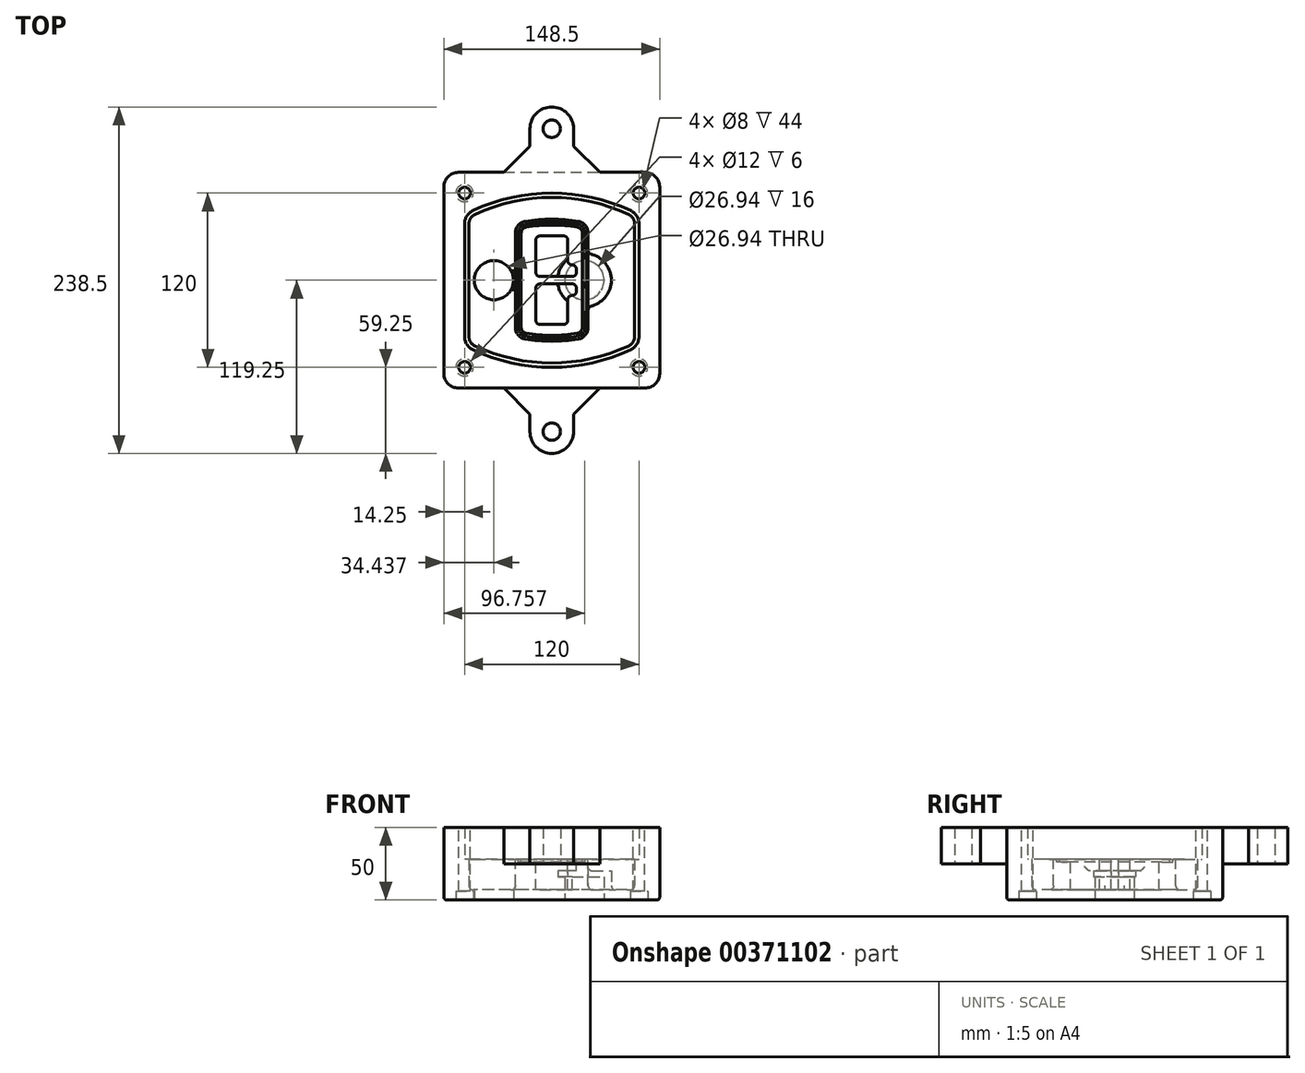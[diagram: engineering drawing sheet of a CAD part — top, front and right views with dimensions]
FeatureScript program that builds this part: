
annotation { "Feature Type Name" : "Feature", "Feature Type Description" : "" }
export const myFeature = defineFeature(function(context is Context, id is Id, definition is map)
    precondition{}
    {
        {
            var Q0;
            Q0=qCreatedBy(makeId("Top.planeOp"),FACE);
            var sketch = newSketch(context, id + "F0", { "sketchPlane" : qUnion([Q0])});
            skPoint(sketch, "E0.rect.middle", {"position": v(0, 0) * mm});
            skLineSegment(sketch, "E1.bottom", {"start": v(-64.25, -74.25) * mm, "end": v(64.25, -74.25) * mm});
            skLineSegment(sketch, "E1.top", {"start": v(-64.25, 74.25) * mm, "end": v(64.25, 74.25) * mm});
            skLineSegment(sketch, "E1.left", {"start": v(-74.25, -64.25) * mm, "end": v(-74.25, 64.25) * mm});
            skLineSegment(sketch, "E1.right", {"start": v(74.25, -64.25) * mm, "end": v(74.25, 64.25) * mm});
            skLineSegment(sketch, "E2", {"start": v(-74.25, 74.25) * mm, "end": v(74.25, -74.25) * mm, "construction": true});
            skLineSegment(sketch, "E3", {"start": v(74.25, 74.25) * mm, "end": v(-74.25, -74.25) * mm, "construction": true});
            skCircle(sketch, "E4", {"center": v(-60, 60) * mm, "radius": 4 * mm});
            skCircle(sketch, "E5", {"center": v(60, 60) * mm, "radius": 4 * mm});
            skCircle(sketch, "E6", {"center": v(60, -60) * mm, "radius": 4 * mm});
            skCircle(sketch, "E7", {"center": v(-60, -60) * mm, "radius": 4 * mm});
            skLineSegment(sketch, "E8", {"start": v(-60, 60) * mm, "end": v(60, 60) * mm, "construction": true});
            skLineSegment(sketch, "E9", {"start": v(60, 60) * mm, "end": v(60, -60) * mm, "construction": true});
            skLineSegment(sketch, "E10", {"start": v(60, -60) * mm, "end": v(-60, -60) * mm, "construction": true});
            skLineSegment(sketch, "E11", {"start": v(-60, -60) * mm, "end": v(-60, 60) * mm, "construction": true});
            skLineSegment(sketch, "E12", {"start": v(-60, 38.83) * mm, "end": v(-60, -38.83) * mm});
            skLineSegment(sketch, "E13", {"start": v(60, 38.83) * mm, "end": v(60, -38.83) * mm});
            skArc(sketch, "E14", {"start": v(54.26, 47.88) * mm, "mid": v(0, 60) * mm, "end": v(-54.26, 47.88) * mm});
            skArc(sketch, "E15", {"start": v(-54.26, -47.88) * mm, "mid": v(0, -60) * mm, "end": v(54.26, -47.88) * mm});
            skLineSegment(sketch, "E16", {"start": v(-60, 0) * mm, "end": v(60, 0) * mm, "construction": true});
            skPoint(sketch, "E17.visualSharp", {"position": v(-60, -45) * mm});
            skArc(sketch, "E17.filletArc", {"start": v(-60, -38.83) * mm, "mid": v(-58.44, -44.2) * mm, "end": v(-54.26, -47.88) * mm});
            skPoint(sketch, "E18.visualSharp", {"position": v(-60, 45) * mm});
            skArc(sketch, "E18.filletArc", {"start": v(-54.26, 47.88) * mm, "mid": v(-58.44, 44.2) * mm, "end": v(-60, 38.83) * mm});
            skPoint(sketch, "E19.visualSharp", {"position": v(60, 45) * mm});
            skArc(sketch, "E19.filletArc", {"start": v(60, 38.83) * mm, "mid": v(58.44, 44.2) * mm, "end": v(54.26, 47.88) * mm});
            skPoint(sketch, "E20.visualSharp", {"position": v(60, -45) * mm});
            skArc(sketch, "E20.filletArc", {"start": v(54.26, -47.88) * mm, "mid": v(58.44, -44.2) * mm, "end": v(60, -38.83) * mm});
            skPoint(sketch, "E21.visualSharp", {"position": v(-74.25, 74.25) * mm});
            skArc(sketch, "E21.filletArc", {"start": v(-64.25, 74.25) * mm, "mid": v(-71.32, 71.32) * mm, "end": v(-74.25, 64.25) * mm});
            skPoint(sketch, "E22.visualSharp", {"position": v(74.25, 74.25) * mm});
            skArc(sketch, "E22.filletArc", {"start": v(74.25, 64.25) * mm, "mid": v(71.32, 71.32) * mm, "end": v(64.25, 74.25) * mm});
            skPoint(sketch, "E23.visualSharp", {"position": v(74.25, -74.25) * mm});
            skArc(sketch, "E23.filletArc", {"start": v(64.25, -74.25) * mm, "mid": v(71.32, -71.32) * mm, "end": v(74.25, -64.25) * mm});
            skPoint(sketch, "E24.visualSharp", {"position": v(-74.25, -74.25) * mm});
            skArc(sketch, "E24.filletArc", {"start": v(-74.25, -64.25) * mm, "mid": v(-71.32, -71.32) * mm, "end": v(-64.25, -74.25) * mm});
            skArc(sketch, "E25.0", {"start": v(57, 38.83) * mm, "mid": v(55.9, 42.58) * mm, "end": v(52.98, 45.17) * mm});
            skLineSegment(sketch, "E25.1", {"start": v(57, 38.83) * mm, "end": v(57, -38.83) * mm});
            skArc(sketch, "E25.2", {"start": v(52.98, -45.17) * mm, "mid": v(55.9, -42.58) * mm, "end": v(57, -38.83) * mm});
            skArc(sketch, "E25.3", {"start": v(-52.98, -45.17) * mm, "mid": v(0, -57) * mm, "end": v(52.98, -45.17) * mm});
            skArc(sketch, "E25.4", {"start": v(-57, -38.83) * mm, "mid": v(-55.9, -42.58) * mm, "end": v(-52.98, -45.17) * mm});
            skArc(sketch, "E25.5", {"start": v(52.98, 45.17) * mm, "mid": v(0, 57) * mm, "end": v(-52.98, 45.17) * mm});
            skLineSegment(sketch, "E25.6", {"start": v(-57, 38.83) * mm, "end": v(-57, -38.83) * mm});
            skArc(sketch, "E25.7", {"start": v(-52.98, 45.17) * mm, "mid": v(-55.9, 42.58) * mm, "end": v(-57, 38.83) * mm});
            skArc(sketch, "E26.0", {"start": v(-55.96, 51.5) * mm, "mid": v(-61.82, 46.33) * mm, "end": v(-64, 38.83) * mm});
            skArc(sketch, "E26.1", {"start": v(55.96, 51.5) * mm, "mid": v(0, 64) * mm, "end": v(-55.96, 51.5) * mm});
            skArc(sketch, "E26.2", {"start": v(64, 38.83) * mm, "mid": v(61.82, 46.33) * mm, "end": v(55.96, 51.5) * mm});
            skLineSegment(sketch, "E26.3", {"start": v(64, 38.83) * mm, "end": v(64, -38.83) * mm});
            skArc(sketch, "E26.4", {"start": v(55.96, -51.5) * mm, "mid": v(61.82, -46.33) * mm, "end": v(64, -38.83) * mm});
            skLineSegment(sketch, "E26.5", {"start": v(-64, 38.83) * mm, "end": v(-64, -38.83) * mm});
            skArc(sketch, "E26.6", {"start": v(-55.96, -51.5) * mm, "mid": v(0, -64) * mm, "end": v(55.96, -51.5) * mm});
            skArc(sketch, "E26.7", {"start": v(-64, -38.83) * mm, "mid": v(-61.82, -46.33) * mm, "end": v(-55.96, -51.5) * mm});
            skSolve(sketch);
        }
        {
            var Q0;
            Q0=makeQuery(id+"F0.imprint","IMPRINT",FACE,{"disambiguationData":[TD([[makeQuery(id+"F0.imprint","IMPRINT",EDGE,{"derivedFrom":sQuery(id+"F0.wireOp",EDGE,"E1.bottom")}),1.0]])]});
            var Q1;
            Q1=makeQuery(id+"F0.imprint","IMPRINT",FACE,{"disambiguationData":[TD([[makeQuery(id+"F0.imprint","IMPRINT",EDGE,{"derivedFrom":sQuery(id+"F0.wireOp",EDGE,"E12")}),1.0]])]});
            var Q2;
            Q2=makeQuery(id+"F0.imprint","IMPRINT",FACE,{"disambiguationData":[TD([[makeQuery(id+"F0.imprint","IMPRINT",EDGE,{"derivedFrom":sQuery(id+"F0.wireOp",EDGE,"E25.0")}),1.0]])]});
            var Q3;
            Q3=makeQuery(id+"F0.imprint","IMPRINT",FACE,{"disambiguationData":[TD([[makeQuery(id+"F0.imprint","IMPRINT",EDGE,{"derivedFrom":sQuery(id+"F0.wireOp",EDGE,"E12")}),-1.0]])]});
            extrude(context, id + "F1", {"entities" : qUnion([Q0, Q1, Q2, Q3]), "oppositeDirection" : true, "depth" : 25 * mm});
        }
        {
            var Q0;
            Q0=makeQuery(id+"F0.imprint","IMPRINT",FACE,{"disambiguationData":[TD([[makeQuery(id+"F0.imprint","IMPRINT",EDGE,{"derivedFrom":sQuery(id+"F0.wireOp",EDGE,"E12")}),1.0]])]});
            extrude(context, id + "F2", {"entities" : qUnion([Q0]), "operationType" : NewBodyOperationType.ADD, "depth" : 3 * mm});
        }
        {
            var Q0;
            Q0=makeQuery(id+"F0.imprint","IMPRINT",FACE,{"disambiguationData":[TD([[makeQuery(id+"F0.imprint","IMPRINT",EDGE,{"derivedFrom":sQuery(id+"F0.wireOp",EDGE,"E25.0")}),1.0]])]});
            extrude(context, id + "F3", {"entities" : qUnion([Q0]), "operationType" : NewBodyOperationType.REMOVE, "oppositeDirection" : true, "depth" : 18 * mm});
        }
        {
            var Q0;
            Q0=makeQuery(id+"F2.opExtrude","CAP_FACE",FACE,{"disambiguationData":[OSD([sQuery(id+"F0.wireOp",EDGE,"E12"),sQuery(id+"F0.wireOp",EDGE,"E13"),sQuery(id+"F0.wireOp",EDGE,"E14"),sQuery(id+"F0.wireOp",EDGE,"E15"),sQuery(id+"F0.wireOp",EDGE,"E17.filletArc"),sQuery(id+"F0.wireOp",EDGE,"E18.filletArc"),sQuery(id+"F0.wireOp",EDGE,"E19.filletArc"),sQuery(id+"F0.wireOp",EDGE,"E20.filletArc"),sQuery(id+"F0.wireOp",EDGE,"E25.0"),sQuery(id+"F0.wireOp",EDGE,"E25.1"),sQuery(id+"F0.wireOp",EDGE,"E25.2"),sQuery(id+"F0.wireOp",EDGE,"E25.3"),sQuery(id+"F0.wireOp",EDGE,"E25.4"),sQuery(id+"F0.wireOp",EDGE,"E25.5"),sQuery(id+"F0.wireOp",EDGE,"E25.6"),sQuery(id+"F0.wireOp",EDGE,"E25.7")])],"isStart":false});
            var sketch = newSketch(context, id + "F4", { "sketchPlane" : qUnion([Q0])});
            skArc(sketch, "E27.0", {"start": v(-18.34, -40.45) * mm, "mid": v(0, -42) * mm, "end": v(18.34, -40.45) * mm});
            skArc(sketch, "E28.0", {"start": v(18.34, 40.45) * mm, "mid": v(0, 42) * mm, "end": v(-18.34, 40.45) * mm});
            skLineSegment(sketch, "E29", {"start": v(-25, 32.57) * mm, "end": v(-25, -32.57) * mm});
            skLineSegment(sketch, "E30", {"start": v(25, 32.57) * mm, "end": v(25, -32.57) * mm});
            skLineSegment(sketch, "E31", {"start": v(-25, 39.1) * mm, "end": v(25, 39.1) * mm, "construction": true});
            skLineSegment(sketch, "E32", {"start": v(-25, -39.1) * mm, "end": v(25, -39.1) * mm, "construction": true});
            skPoint(sketch, "E33.visualSharp", {"position": v(-25, 39.1) * mm});
            skArc(sketch, "E33.filletArc", {"start": v(-18.34, 40.45) * mm, "mid": v(-23.11, 37.73) * mm, "end": v(-25, 32.57) * mm});
            skPoint(sketch, "E34.visualSharp", {"position": v(25, 39.1) * mm});
            skArc(sketch, "E34.filletArc", {"start": v(25, 32.57) * mm, "mid": v(23.11, 37.73) * mm, "end": v(18.34, 40.45) * mm});
            skPoint(sketch, "E35.visualSharp", {"position": v(25, -39.1) * mm});
            skArc(sketch, "E35.filletArc", {"start": v(18.34, -40.45) * mm, "mid": v(23.11, -37.73) * mm, "end": v(25, -32.57) * mm});
            skPoint(sketch, "E36.visualSharp", {"position": v(-25, -39.1) * mm});
            skArc(sketch, "E36.filletArc", {"start": v(-25, -32.57) * mm, "mid": v(-23.11, -37.73) * mm, "end": v(-18.34, -40.45) * mm});
            skArc(sketch, "E37.0", {"start": v(52.98, 45.17) * mm, "mid": v(0, 57) * mm, "end": v(-52.98, 45.17) * mm});
            skArc(sketch, "E37.1", {"start": v(-52.98, 45.17) * mm, "mid": v(-55.9, 42.58) * mm, "end": v(-57, 38.83) * mm});
            skLineSegment(sketch, "E37.2", {"start": v(-57, 38.83) * mm, "end": v(-57, -38.83) * mm});
            skArc(sketch, "E37.3", {"start": v(-57, -38.83) * mm, "mid": v(-55.9, -42.58) * mm, "end": v(-52.98, -45.17) * mm});
            skArc(sketch, "E37.4", {"start": v(-52.98, -45.17) * mm, "mid": v(0, -57) * mm, "end": v(52.98, -45.17) * mm});
            skArc(sketch, "E37.5", {"start": v(52.98, -45.17) * mm, "mid": v(55.9, -42.58) * mm, "end": v(57, -38.83) * mm});
            skLineSegment(sketch, "E37.6", {"start": v(57, 38.83) * mm, "end": v(57, -38.83) * mm});
            skArc(sketch, "E37.7", {"start": v(57, 38.83) * mm, "mid": v(55.9, 42.58) * mm, "end": v(52.98, 45.17) * mm});
            skLineSegment(sketch, "E38.0", {"start": v(23, 32.57) * mm, "end": v(23, -32.57) * mm});
            skArc(sketch, "E38.1", {"start": v(18, -38.48) * mm, "mid": v(21.58, -36.44) * mm, "end": v(23, -32.57) * mm});
            skArc(sketch, "E38.2", {"start": v(-18, -38.48) * mm, "mid": v(0, -40) * mm, "end": v(18, -38.48) * mm});
            skArc(sketch, "E38.3", {"start": v(-23, -32.57) * mm, "mid": v(-21.58, -36.44) * mm, "end": v(-18, -38.48) * mm});
            skLineSegment(sketch, "E38.4", {"start": v(-23, 32.57) * mm, "end": v(-23, -32.57) * mm});
            skArc(sketch, "E38.5", {"start": v(23, 32.57) * mm, "mid": v(21.58, 36.44) * mm, "end": v(18, 38.48) * mm});
            skArc(sketch, "E38.6", {"start": v(-18, 38.48) * mm, "mid": v(-21.58, 36.44) * mm, "end": v(-23, 32.57) * mm});
            skArc(sketch, "E38.7", {"start": v(18, 38.48) * mm, "mid": v(0, 40) * mm, "end": v(-18, 38.48) * mm});
            skArc(sketch, "E39.0", {"start": v(21, 32.57) * mm, "mid": v(20.06, 35.15) * mm, "end": v(17.67, 36.5) * mm});
            skLineSegment(sketch, "E39.1", {"start": v(21, 32.57) * mm, "end": v(21, -32.57) * mm});
            skArc(sketch, "E39.2", {"start": v(17.67, -36.5) * mm, "mid": v(20.06, -35.15) * mm, "end": v(21, -32.57) * mm});
            skArc(sketch, "E39.3", {"start": v(-17.67, -36.5) * mm, "mid": v(0, -38) * mm, "end": v(17.67, -36.5) * mm});
            skArc(sketch, "E39.4", {"start": v(-21, -32.57) * mm, "mid": v(-20.06, -35.15) * mm, "end": v(-17.67, -36.5) * mm});
            skArc(sketch, "E39.5", {"start": v(17.67, 36.5) * mm, "mid": v(0, 38) * mm, "end": v(-17.67, 36.5) * mm});
            skLineSegment(sketch, "E39.6", {"start": v(-21, 32.57) * mm, "end": v(-21, -32.57) * mm});
            skArc(sketch, "E39.7", {"start": v(-17.67, 36.5) * mm, "mid": v(-20.06, 35.15) * mm, "end": v(-21, 32.57) * mm});
            skLineSegment(sketch, "E40", {"start": v(-25, 0) * mm, "end": v(25, 0) * mm, "construction": true});
            skLineSegment(sketch, "E41", {"start": v(-11, 5.5) * mm, "end": v(-11, 27.5) * mm});
            skLineSegment(sketch, "E42", {"start": v(-8, 30.5) * mm, "end": v(8, 30.5) * mm});
            skLineSegment(sketch, "E43", {"start": v(11, 27.5) * mm, "end": v(11, 13.5) * mm});
            skLineSegment(sketch, "E44", {"start": v(14, 10.5) * mm, "end": v(14, 10.5) * mm});
            skLineSegment(sketch, "E45", {"start": v(17, 7.5) * mm, "end": v(17, 5.5) * mm});
            skLineSegment(sketch, "E46", {"start": v(14, 2.5) * mm, "end": v(-8, 2.5) * mm});
            skPoint(sketch, "E47.visualSharp", {"position": v(-11, 30.5) * mm});
            skArc(sketch, "E47.filletArc", {"start": v(-8, 30.5) * mm, "mid": v(-10.12, 29.62) * mm, "end": v(-11, 27.5) * mm});
            skPoint(sketch, "E48.visualSharp", {"position": v(11, 30.5) * mm});
            skArc(sketch, "E48.filletArc", {"start": v(11, 27.5) * mm, "mid": v(10.12, 29.62) * mm, "end": v(8, 30.5) * mm});
            skPoint(sketch, "E49.visualSharp", {"position": v(11, 10.5) * mm});
            skArc(sketch, "E49.filletArc", {"start": v(11, 13.5) * mm, "mid": v(11.88, 11.38) * mm, "end": v(14, 10.5) * mm});
            skPoint(sketch, "E50.visualSharp", {"position": v(17, 10.5) * mm});
            skArc(sketch, "E50.filletArc", {"start": v(17, 7.5) * mm, "mid": v(16.12, 9.62) * mm, "end": v(14, 10.5) * mm});
            skPoint(sketch, "E51.visualSharp", {"position": v(17, 2.5) * mm});
            skArc(sketch, "E51.filletArc", {"start": v(14, 2.5) * mm, "mid": v(16.12, 3.38) * mm, "end": v(17, 5.5) * mm});
            skPoint(sketch, "E52.visualSharp", {"position": v(-11, 2.5) * mm});
            skArc(sketch, "E52.filletArc", {"start": v(-11, 5.5) * mm, "mid": v(-10.12, 3.38) * mm, "end": v(-8, 2.5) * mm});
            skLineSegment(sketch, "E53.0.MirrorCS", {"start": v(14, -2.5) * mm, "end": v(-8, -2.5) * mm});
            skArc(sketch, "E54.0.MirrorCS", {"start": v(-11, -5.5) * mm, "mid": v(-10.12, -3.38) * mm, "end": v(-8, -2.5) * mm});
            skLineSegment(sketch, "E55.0.MirrorCS", {"start": v(-11, -5.5) * mm, "end": v(-11, -27.5) * mm});
            skArc(sketch, "E56.0.MirrorCS", {"start": v(-8, -30.5) * mm, "mid": v(-10.12, -29.62) * mm, "end": v(-11, -27.5) * mm});
            skLineSegment(sketch, "E57.0.MirrorCS", {"start": v(-8, -30.5) * mm, "end": v(8, -30.5) * mm});
            skArc(sketch, "E58.0.MirrorCS", {"start": v(11, -27.5) * mm, "mid": v(10.12, -29.62) * mm, "end": v(8, -30.5) * mm});
            skLineSegment(sketch, "E59.0.MirrorCS", {"start": v(11, -27.5) * mm, "end": v(11, -13.5) * mm});
            skArc(sketch, "E60.0.MirrorCS", {"start": v(11, -13.5) * mm, "mid": v(11.88, -11.38) * mm, "end": v(14, -10.5) * mm});
            skArc(sketch, "E61.0.MirrorCS", {"start": v(17, -7.5) * mm, "mid": v(16.12, -9.62) * mm, "end": v(14, -10.5) * mm});
            skLineSegment(sketch, "E62.0.MirrorCS", {"start": v(17, -7.5) * mm, "end": v(17, -5.5) * mm});
            skArc(sketch, "E63.0.MirrorCS", {"start": v(14, -2.5) * mm, "mid": v(16.12, -3.38) * mm, "end": v(17, -5.5) * mm});
            skSolve(sketch);
        }
        {
            var Q0;
            Q0=makeQuery(id+"F4.imprint","IMPRINT",FACE,{"disambiguationData":[TD([[makeQuery(id+"F4.imprint","IMPRINT",EDGE,{"derivedFrom":sQuery(id+"F4.wireOp",EDGE,"E27.0")}),1.0]])]});
            var Q1;
            Q1=makeQuery(id+"F4.imprint","IMPRINT",FACE,{"disambiguationData":[TD([[makeQuery(id+"F4.imprint","IMPRINT",EDGE,{"derivedFrom":sQuery(id+"F4.wireOp",EDGE,"E38.0")}),-1.0]])]});
            var Q2;
            Q2=makeQuery(id+"F4.imprint","IMPRINT",FACE,{"disambiguationData":[TD([[makeQuery(id+"F4.imprint","IMPRINT",EDGE,{"derivedFrom":sQuery(id+"F4.wireOp",EDGE,"E39.0")}),1.0]])]});
            extrude(context, id + "F5", {"entities" : qUnion([Q0, Q1, Q2]), "operationType" : NewBodyOperationType.ADD, "endBound" : BoundingType.UP_TO_NEXT, "oppositeDirection" : true, "depth" : 25 * mm});
        }
        {
            var Q0;
            Q0=makeQuery(id+"F4.imprint","IMPRINT",FACE,{"disambiguationData":[TD([[makeQuery(id+"F4.imprint","IMPRINT",EDGE,{"derivedFrom":sQuery(id+"F4.wireOp",EDGE,"E38.0")}),-1.0]])]});
            extrude(context, id + "F6", {"entities" : qUnion([Q0]), "operationType" : NewBodyOperationType.REMOVE, "oppositeDirection" : true, "depth" : 2 * mm});
        }
        {
            var Q0;
            Q0=makeQuery(id+"F1.opExtrude","CAP_FACE",FACE,{"disambiguationData":[OSD([sQuery(id+"F0.wireOp",EDGE,"E1.bottom"),sQuery(id+"F0.wireOp",EDGE,"E1.top"),sQuery(id+"F0.wireOp",EDGE,"E1.left"),sQuery(id+"F0.wireOp",EDGE,"E1.right"),sQuery(id+"F0.wireOp",EDGE,"E4"),sQuery(id+"F0.wireOp",EDGE,"E5"),sQuery(id+"F0.wireOp",EDGE,"E6"),sQuery(id+"F0.wireOp",EDGE,"E7"),sQuery(id+"F0.wireOp",EDGE,"E21.filletArc"),sQuery(id+"F0.wireOp",EDGE,"E22.filletArc"),sQuery(id+"F0.wireOp",EDGE,"E23.filletArc"),sQuery(id+"F0.wireOp",EDGE,"E24.filletArc")])],"isStart":false});
            var sketch = newSketch(context, id + "F7", { "sketchPlane" : qUnion([Q0])});
            skCircle(sketch, "E64", {"center": v(22.5, 0) * mm, "radius": 13.47 * mm});
            skCircle(sketch, "E65", {"center": v(-39.81, 0) * mm, "radius": 13.47 * mm});
            skLineSegment(sketch, "E66", {"start": v(74.25, 0) * mm, "end": v(-74.25, 0) * mm});
            skCircle(sketch, "E67", {"center": v(22.5, 0) * mm, "radius": 18.47 * mm});
            skCircle(sketch, "E68", {"center": v(60, -60) * mm, "radius": 6 * mm});
            skCircle(sketch, "E69", {"center": v(-60, -60) * mm, "radius": 6 * mm});
            skCircle(sketch, "E70", {"center": v(-60, 60) * mm, "radius": 6 * mm});
            skCircle(sketch, "E71", {"center": v(60, 60) * mm, "radius": 6 * mm});
            skSolve(sketch);
        }
        {
            var Q0;
            {var subQ1=sQuery(id+"F7.wireOp",EDGE,"E66");var subQ4=sQuery(id+"F7.wireOp",EDGE,"E64");var subQ6=makeQuery(id+"F7.imprint","INTERSECT",VERTEX,{"disambiguationData":[OD(0.0)],"derivedFrom":[subQ4,subQ1]});Q0=makeQuery(id+"F7.imprint","IMPRINT",FACE,{"disambiguationData":[TD([[makeQuery(id+"F7.imprint","IMPRINT",EDGE,{"disambiguationData":[TD([[subQ6,-1.0]])],"derivedFrom":subQ4}),-1.0]])]});}
            var Q1;
            {var subQ0=sQuery(id+"F7.wireOp",EDGE,"E66");var subQ1=sQuery(id+"F7.wireOp",EDGE,"E64");var subQ3=makeQuery(id+"F7.imprint","INTERSECT",VERTEX,{"disambiguationData":[OD(0.0)],"derivedFrom":[subQ1,subQ0]});Q1=makeQuery(id+"F7.imprint","IMPRINT",FACE,{"disambiguationData":[TD([[makeQuery(id+"F7.imprint","IMPRINT",EDGE,{"disambiguationData":[TD([[subQ3,-1.0]])],"derivedFrom":subQ1}),1.0]])]});}
            var Q2;
            {var subQ0=sQuery(id+"F7.wireOp",EDGE,"E66");var subQ1=sQuery(id+"F7.wireOp",EDGE,"E64");var subQ3=makeQuery(id+"F7.imprint","INTERSECT",VERTEX,{"disambiguationData":[OD(0.0)],"derivedFrom":[subQ1,subQ0]});Q2=makeQuery(id+"F7.imprint","IMPRINT",FACE,{"disambiguationData":[TD([[makeQuery(id+"F7.imprint","IMPRINT",EDGE,{"disambiguationData":[TD([[subQ3,1.0]])],"derivedFrom":subQ1}),1.0]])]});}
            var Q3;
            {var subQ1=sQuery(id+"F7.wireOp",EDGE,"E66");var subQ4=sQuery(id+"F7.wireOp",EDGE,"E64");var subQ6=makeQuery(id+"F7.imprint","INTERSECT",VERTEX,{"disambiguationData":[OD(0.0)],"derivedFrom":[subQ4,subQ1]});Q3=makeQuery(id+"F7.imprint","IMPRINT",FACE,{"disambiguationData":[TD([[makeQuery(id+"F7.imprint","IMPRINT",EDGE,{"disambiguationData":[TD([[subQ6,1.0]])],"derivedFrom":subQ4}),-1.0]])]});}
            extrude(context, id + "F8", {"entities" : qUnion([Q0, Q1, Q2, Q3]), "operationType" : NewBodyOperationType.ADD, "oppositeDirection" : true, "depth" : 20 * mm});
        }
        {
            var Q0;
            {var subQ0=sQuery(id+"F7.wireOp",EDGE,"E66");var subQ1=sQuery(id+"F7.wireOp",EDGE,"E64");var subQ3=makeQuery(id+"F7.imprint","INTERSECT",VERTEX,{"disambiguationData":[OD(0.0)],"derivedFrom":[subQ1,subQ0]});Q0=makeQuery(id+"F7.imprint","IMPRINT",FACE,{"disambiguationData":[TD([[makeQuery(id+"F7.imprint","IMPRINT",EDGE,{"disambiguationData":[TD([[subQ3,-1.0]])],"derivedFrom":subQ1}),1.0]])]});}
            var Q1;
            {var subQ0=sQuery(id+"F7.wireOp",EDGE,"E66");var subQ1=sQuery(id+"F7.wireOp",EDGE,"E64");var subQ3=makeQuery(id+"F7.imprint","INTERSECT",VERTEX,{"disambiguationData":[OD(0.0)],"derivedFrom":[subQ1,subQ0]});Q1=makeQuery(id+"F7.imprint","IMPRINT",FACE,{"disambiguationData":[TD([[makeQuery(id+"F7.imprint","IMPRINT",EDGE,{"disambiguationData":[TD([[subQ3,1.0]])],"derivedFrom":subQ1}),1.0]])]});}
            extrude(context, id + "F9", {"entities" : qUnion([Q0, Q1]), "operationType" : NewBodyOperationType.REMOVE, "oppositeDirection" : true, "depth" : 16 * mm});
        }
        {
            var Q0;
            {var subQ0=sQuery(id+"F7.wireOp",EDGE,"E66");var subQ1=sQuery(id+"F7.wireOp",EDGE,"E65");var subQ3=makeQuery(id+"F7.imprint","INTERSECT",VERTEX,{"disambiguationData":[OD(0.0)],"derivedFrom":[subQ1,subQ0]});Q0=makeQuery(id+"F7.imprint","IMPRINT",FACE,{"disambiguationData":[TD([[makeQuery(id+"F7.imprint","IMPRINT",EDGE,{"disambiguationData":[TD([[subQ3,-1.0]])],"derivedFrom":subQ1}),1.0]])]});}
            var Q1;
            {var subQ0=sQuery(id+"F7.wireOp",EDGE,"E66");var subQ1=sQuery(id+"F7.wireOp",EDGE,"E65");var subQ3=makeQuery(id+"F7.imprint","INTERSECT",VERTEX,{"disambiguationData":[OD(0.0)],"derivedFrom":[subQ1,subQ0]});Q1=makeQuery(id+"F7.imprint","IMPRINT",FACE,{"disambiguationData":[TD([[makeQuery(id+"F7.imprint","IMPRINT",EDGE,{"disambiguationData":[TD([[subQ3,1.0]])],"derivedFrom":subQ1}),1.0]])]});}
            extrude(context, id + "F10", {"entities" : qUnion([Q0, Q1]), "operationType" : NewBodyOperationType.REMOVE, "oppositeDirection" : true, "depth" : 25 * mm});
        }
        {
            var Q0;
            Q0=makeQuery(id+"F7.imprint","IMPRINT",FACE,{"disambiguationData":[TD([[makeQuery(id+"F7.imprint","IMPRINT",EDGE,{"derivedFrom":sQuery(id+"F7.wireOp",EDGE,"E68")}),1.0]])]});
            var Q1;
            Q1=makeQuery(id+"F7.imprint","IMPRINT",FACE,{"disambiguationData":[TD([[makeQuery(id+"F7.imprint","IMPRINT",EDGE,{"derivedFrom":makeQuery(id+"F1.opExtrude","CAP_EDGE",EDGE,{"disambiguationData":[OSD([sQuery(id+"F0.wireOp",EDGE,"E5")])],"isStart":false})}),-1.0]])]});
            var Q2;
            Q2=makeQuery(id+"F7.imprint","IMPRINT",FACE,{"disambiguationData":[TD([[makeQuery(id+"F7.imprint","IMPRINT",EDGE,{"derivedFrom":sQuery(id+"F7.wireOp",EDGE,"E69")}),1.0]])]});
            var Q3;
            Q3=makeQuery(id+"F7.imprint","IMPRINT",FACE,{"disambiguationData":[TD([[makeQuery(id+"F7.imprint","IMPRINT",EDGE,{"derivedFrom":makeQuery(id+"F1.opExtrude","CAP_EDGE",EDGE,{"disambiguationData":[OSD([sQuery(id+"F0.wireOp",EDGE,"E4")])],"isStart":false})}),-1.0]])]});
            var Q4;
            Q4=makeQuery(id+"F7.imprint","IMPRINT",FACE,{"disambiguationData":[TD([[makeQuery(id+"F7.imprint","IMPRINT",EDGE,{"derivedFrom":sQuery(id+"F7.wireOp",EDGE,"E70")}),1.0]])]});
            var Q5;
            Q5=makeQuery(id+"F7.imprint","IMPRINT",FACE,{"disambiguationData":[TD([[makeQuery(id+"F7.imprint","IMPRINT",EDGE,{"derivedFrom":makeQuery(id+"F1.opExtrude","CAP_EDGE",EDGE,{"disambiguationData":[OSD([sQuery(id+"F0.wireOp",EDGE,"E7")])],"isStart":false})}),-1.0]])]});
            var Q6;
            Q6=makeQuery(id+"F7.imprint","IMPRINT",FACE,{"disambiguationData":[TD([[makeQuery(id+"F7.imprint","IMPRINT",EDGE,{"derivedFrom":sQuery(id+"F7.wireOp",EDGE,"E71")}),1.0]])]});
            var Q7;
            Q7=makeQuery(id+"F7.imprint","IMPRINT",FACE,{"disambiguationData":[TD([[makeQuery(id+"F7.imprint","IMPRINT",EDGE,{"derivedFrom":makeQuery(id+"F1.opExtrude","CAP_EDGE",EDGE,{"disambiguationData":[OSD([sQuery(id+"F0.wireOp",EDGE,"E6")])],"isStart":false})}),-1.0]])]});
            extrude(context, id + "F11", {"entities" : qUnion([Q0, Q1, Q2, Q3, Q4, Q5, Q6, Q7]), "operationType" : NewBodyOperationType.REMOVE, "oppositeDirection" : true, "depth" : 6 * mm});
        }
        {
            var Q0;
            Q0=makeQuery(id+"F9.boolean.opBoolean","COPY",FACE,{"derivedFrom":makeQuery(id+"F9.opExtrude","CAP_FACE",FACE,{"disambiguationData":[OSD([sQuery(id+"F7.wireOp",EDGE,"E64")])],"isStart":false})});
            var sketch = newSketch(context, id + "F12", { "sketchPlane" : qUnion([Q0])});
            skArc(sketch, "E72.0", {"start": v(11, 14.45) * mm, "mid": v(6.45, 9.13) * mm, "end": v(4.2, 2.5) * mm});
            skArc(sketch, "E72.1", {"start": v(4.2, -2.5) * mm, "mid": v(6.45, -9.13) * mm, "end": v(11, -14.45) * mm});
            skLineSegment(sketch, "E73", {"start": v(4.2, -2.5) * mm, "end": v(14, -2.5) * mm});
            skLineSegment(sketch, "E74.0", {"start": v(14, 2.5) * mm, "end": v(4.2, 2.5) * mm});
            skArc(sketch, "E74.1", {"start": v(14, 2.5) * mm, "mid": v(16.12, 3.38) * mm, "end": v(17, 5.5) * mm});
            skLineSegment(sketch, "E74.2", {"start": v(17, 7.5) * mm, "end": v(17, 5.5) * mm});
            skArc(sketch, "E74.3", {"start": v(17, 7.5) * mm, "mid": v(16.12, 9.62) * mm, "end": v(14, 10.5) * mm});
            skArc(sketch, "E74.4", {"start": v(11, 13.5) * mm, "mid": v(11.88, 11.38) * mm, "end": v(14, 10.5) * mm});
            skLineSegment(sketch, "E74.5", {"start": v(11, 14.45) * mm, "end": v(11, 13.5) * mm});
            skLineSegment(sketch, "E74.7", {"start": v(14, -2.5) * mm, "end": v(4.2, -2.5) * mm});
            skArc(sketch, "E74.8", {"start": v(14, -2.5) * mm, "mid": v(16.12, -3.38) * mm, "end": v(17, -5.5) * mm});
            skLineSegment(sketch, "E74.9", {"start": v(17, -7.5) * mm, "end": v(17, -5.5) * mm});
            skArc(sketch, "E74.10", {"start": v(17, -7.5) * mm, "mid": v(16.12, -9.62) * mm, "end": v(14, -10.5) * mm});
            skArc(sketch, "E74.11", {"start": v(11, -13.5) * mm, "mid": v(11.88, -11.38) * mm, "end": v(14, -10.5) * mm});
            skLineSegment(sketch, "E74.12", {"start": v(11, -14.45) * mm, "end": v(11, -13.5) * mm});
            skPoint(sketch, "E75.orphan", {"position": v(11, -27.5) * mm});
            skPoint(sketch, "E76.orphan", {"position": v(-8, -2.5) * mm});
            skPoint(sketch, "E77.orphan", {"position": v(-8, 2.5) * mm});
            skPoint(sketch, "E78.orphan", {"position": v(11, 27.5) * mm});
            skSolve(sketch);
        }
        {
            var Q0;
            {var subQ7=sQuery(id+"F12.wireOp",EDGE,"E72.0");var subQ14=sQuery(id+"F12.wireOp",EDGE,"E72.1");var subQ16=sQuery(id+"F12.wireOp",EDGE,"E74.1");var subQ18=sQuery(id+"F12.wireOp",EDGE,"E74.8");Q0=qUnion([makeQuery(id+"F12.imprint","IMPRINT",FACE,{"disambiguationData":[TD([[makeQuery(id+"F12.imprint","IMPRINT",EDGE,{"derivedFrom":subQ7}),1.0]])]}),makeQuery(id+"F12.imprint","IMPRINT",FACE,{"disambiguationData":[TD([[makeQuery(id+"F12.imprint","IMPRINT",EDGE,{"derivedFrom":subQ14}),1.0]])]}),makeQuery(id+"F12.imprint","IMPRINT",FACE,{"disambiguationData":[TD([[makeQuery(id+"F12.imprint","IMPRINT",EDGE,{"derivedFrom":subQ16}),1.0]])]}),makeQuery(id+"F12.imprint","IMPRINT",FACE,{"disambiguationData":[TD([[makeQuery(id+"F12.imprint","IMPRINT",EDGE,{"derivedFrom":subQ18}),-1.0]])]})]);}
            var Q1;
            Q1=makeQuery(id+"F5.boolean.opBoolean","SPLIT",FACE,{"disambiguationData":[TD([makeQuery(id+"F5.opExtrude","SWEPT_FACE",FACE,{"disambiguationData":[OSD([sQuery(id+"F4.wireOp",EDGE,"E41")])]})])],"derivedFrom":makeQuery(id+"F3.boolean.opBoolean","COPY",FACE,{"derivedFrom":makeQuery(id+"F3.opExtrude","CAP_FACE",FACE,{"disambiguationData":[OSD([sQuery(id+"F0.wireOp",EDGE,"E25.0"),sQuery(id+"F0.wireOp",EDGE,"E25.1"),sQuery(id+"F0.wireOp",EDGE,"E25.2"),sQuery(id+"F0.wireOp",EDGE,"E25.3"),sQuery(id+"F0.wireOp",EDGE,"E25.4"),sQuery(id+"F0.wireOp",EDGE,"E25.5"),sQuery(id+"F0.wireOp",EDGE,"E25.6"),sQuery(id+"F0.wireOp",EDGE,"E25.7")])],"isStart":false})})});
            extrude(context, id + "F13", {"entities" : qUnion([Q0]), "operationType" : NewBodyOperationType.REMOVE, "endBound" : BoundingType.UP_TO_SURFACE, "endBoundEntityFace" : qUnion([Q1]), "depth" : 25 * mm});
        }
        {
            var Q0;
            Q0=makeQuery(id+"F3.boolean.opBoolean","COPY",EDGE,{"derivedFrom":makeQuery(id+"F3.opExtrude","CAP_EDGE",EDGE,{"disambiguationData":[OSD([sQuery(id+"F0.wireOp",EDGE,"E25.6")])],"isStart":false})});
            var Q1;
            Q1=makeQuery(id+"F8.boolean.opBoolean","INTERSECT",EDGE,{"derivedFrom":[makeQuery(id+"F5.opExtrude","SWEPT_FACE",FACE,{"disambiguationData":[OSD([sQuery(id+"F4.wireOp",EDGE,"E30")])]}),makeQuery(id+"F8.opExtrude","CAP_FACE",FACE,{"disambiguationData":[OSD([sQuery(id+"F7.wireOp",EDGE,"E67")])],"isStart":false})]});
            var Q2;
            Q2=makeQuery(id+"F8.boolean.opBoolean","INTERSECT",EDGE,{"disambiguationData":[OD(1.0)],"derivedFrom":[makeQuery(id+"F5.opExtrude","SWEPT_FACE",FACE,{"disambiguationData":[OSD([sQuery(id+"F4.wireOp",EDGE,"E30")])]}),makeQuery(id+"F8.opExtrude","SWEPT_FACE",FACE,{"disambiguationData":[OSD([sQuery(id+"F7.wireOp",EDGE,"E67")])]})]});
            var Q3;
            {var subQ0=sQuery(id+"F4.wireOp",EDGE,"E30");Q3=makeQuery(id+"F8.boolean.opBoolean","SPLIT",EDGE,{"disambiguationData":[TD([makeQuery(id+"F5.opExtrude","SWEPT_FACE",FACE,{"disambiguationData":[OSD([sQuery(id+"F4.wireOp",EDGE,"E35.filletArc")])]})])],"derivedFrom":makeQuery(id+"F5.opExtrude","CAP_EDGE",EDGE,{"disambiguationData":[OSD([subQ0])],"isStart":false})});}
            var Q4;
            {var subQ0=sQuery(id+"F0.wireOp",EDGE,"E25.7");var subQ1=sQuery(id+"F0.wireOp",EDGE,"E25.1");var subQ2=sQuery(id+"F0.wireOp",EDGE,"E25.6");var subQ3=sQuery(id+"F0.wireOp",EDGE,"E25.5");var subQ4=sQuery(id+"F0.wireOp",EDGE,"E25.4");var subQ5=sQuery(id+"F0.wireOp",EDGE,"E25.0");var subQ6=sQuery(id+"F0.wireOp",EDGE,"E25.2");var subQ7=sQuery(id+"F0.wireOp",EDGE,"E25.3");Q4=makeQuery(id+"F8.boolean.opBoolean","INTERSECT",EDGE,{"derivedFrom":[makeQuery(id+"F5.boolean.opBoolean","SPLIT",FACE,{"disambiguationData":[TD([makeQuery(id+"F2.opExtrude","SWEPT_FACE",FACE,{"disambiguationData":[OSD([subQ5])]})])],"derivedFrom":makeQuery(id+"F3.boolean.opBoolean","COPY",FACE,{"derivedFrom":makeQuery(id+"F3.opExtrude","CAP_FACE",FACE,{"disambiguationData":[OSD([subQ5,subQ1,subQ6,subQ7,subQ4,subQ3,subQ2,subQ0])],"isStart":false})})}),makeQuery(id+"F8.opExtrude","SWEPT_FACE",FACE,{"disambiguationData":[OSD([sQuery(id+"F7.wireOp",EDGE,"E67")])]})]});}
            var Q5;
            Q5=makeQuery(id+"F8.boolean.opBoolean","INTERSECT",EDGE,{"disambiguationData":[OD(0.0)],"derivedFrom":[makeQuery(id+"F5.opExtrude","SWEPT_FACE",FACE,{"disambiguationData":[OSD([sQuery(id+"F4.wireOp",EDGE,"E30")])]}),makeQuery(id+"F8.opExtrude","SWEPT_FACE",FACE,{"disambiguationData":[OSD([sQuery(id+"F7.wireOp",EDGE,"E67")])]})]});
            fillet(context, id + "F14", {"entities" : qUnion([Q0, Q1, Q2, Q3, Q4, Q5]), "radius" : 3 * mm, "tangentPropagation" : true, "allowEdgeOverflow" : false});
        }
        {
            var Q0;
            Q0=makeQuery(id+"F1.opExtrude","CAP_EDGE",EDGE,{"disambiguationData":[OSD([sQuery(id+"F0.wireOp",EDGE,"E1.bottom")])],"isStart":false});
            fillet(context, id + "F15", {"entities" : qUnion([Q0]), "radius" : 2 * mm, "tangentPropagation" : true, "allowEdgeOverflow" : false});
        }
        {
            var Q0;
            {var subQ0=sQuery(id+"F0.wireOp",EDGE,"E21.filletArc");var subQ1=sQuery(id+"F0.wireOp",EDGE,"E7");var subQ2=sQuery(id+"F0.wireOp",EDGE,"E6");var subQ3=sQuery(id+"F0.wireOp",EDGE,"E5");var subQ4=sQuery(id+"F0.wireOp",EDGE,"E4");var subQ5=sQuery(id+"F0.wireOp",EDGE,"E22.filletArc");var subQ6=sQuery(id+"F0.wireOp",EDGE,"E1.bottom");var subQ7=sQuery(id+"F0.wireOp",EDGE,"E1.right");var subQ8=sQuery(id+"F0.wireOp",EDGE,"E1.top");var subQ9=sQuery(id+"F0.wireOp",EDGE,"E1.left");var subQ10=sQuery(id+"F0.wireOp",EDGE,"E23.filletArc");var subQ11=sQuery(id+"F0.wireOp",EDGE,"E24.filletArc");Q0=makeQuery(id+"F2.boolean.opBoolean","SPLIT",FACE,{"disambiguationData":[TD([makeQuery(id+"F1.opExtrude","SWEPT_FACE",FACE,{"disambiguationData":[OSD([subQ6])]})])],"derivedFrom":makeQuery(id+"F1.opExtrude","CAP_FACE",FACE,{"disambiguationData":[OSD([subQ6,subQ8,subQ9,subQ7,subQ4,subQ3,subQ2,subQ1,subQ0,subQ5,subQ10,subQ11])],"isStart":true})});}
            var sketch = newSketch(context, id + "F16", { "sketchPlane" : qUnion([Q0])});
            skLineSegment(sketch, "E79", {"start": v(-33, 74.25) * mm, "end": v(-15, 92.25) * mm});
            skLineSegment(sketch, "E80", {"start": v(-15, 92.25) * mm, "end": v(-15, 104.25) * mm});
            skArc(sketch, "E81", {"start": v(-15, 104.25) * mm, "mid": v(0, 119.25) * mm, "end": v(15, 104.25) * mm});
            skCircle(sketch, "E82", {"center": v(0, 104.25) * mm, "radius": 6 * mm});
            skLineSegment(sketch, "E83.MirrorCS", {"start": v(15, 92.25) * mm, "end": v(15, 104.25) * mm});
            skLineSegment(sketch, "E84.MirrorCS", {"start": v(33, 74.25) * mm, "end": v(15, 92.25) * mm});
            skLineSegment(sketch, "E85", {"start": v(-74.25, 0) * mm, "end": v(74.25, 0) * mm});
            skLineSegment(sketch, "E86.MirrorCS", {"start": v(33, -74.25) * mm, "end": v(15, -92.25) * mm});
            skLineSegment(sketch, "E87.MirrorCS", {"start": v(15, -92.25) * mm, "end": v(15, -104.25) * mm});
            skArc(sketch, "E88.MirrorCS", {"start": v(-15, -104.25) * mm, "mid": v(0, -119.25) * mm, "end": v(15, -104.25) * mm});
            skLineSegment(sketch, "E89.MirrorCS", {"start": v(-15, -92.25) * mm, "end": v(-15, -104.25) * mm});
            skLineSegment(sketch, "E90.MirrorCS", {"start": v(-33, -74.25) * mm, "end": v(-15, -92.25) * mm});
            skCircle(sketch, "E91.MirrorC", {"center": v(0, -104.25) * mm, "radius": 6 * mm});
            skSolve(sketch);
        }
        {
            var Q0;
            Q0 = qSketchRegion(id + "F16", true);
            var Q1;
            {var subQ0=sQuery(id+"F16.wireOp",EDGE,"E79");Q1=makeQuery(id+"F16.imprint","IMPRINT",FACE,{"disambiguationData":[TD([[makeQuery(id+"F16.imprint","IMPRINT",EDGE,{"derivedFrom":subQ0}),-1.0]])]});}
            var Q2;
            Q2=makeQuery(id+"F16.imprint","IMPRINT",FACE,{"disambiguationData":[TD([[makeQuery(id+"F16.imprint","IMPRINT",EDGE,{"derivedFrom":makeQuery(id+"F1.opExtrude","CAP_EDGE",EDGE,{"disambiguationData":[OSD([sQuery(id+"F0.wireOp",EDGE,"E4")])],"isStart":true})}),-1.0]])]});
            var Q3;
            Q3=makeQuery(id+"F16.imprint","IMPRINT",FACE,{"disambiguationData":[TD([[makeQuery(id+"F16.imprint","IMPRINT",EDGE,{"derivedFrom":makeQuery(id+"F1.opExtrude","CAP_EDGE",EDGE,{"disambiguationData":[OSD([sQuery(id+"F0.wireOp",EDGE,"E6")])],"isStart":true})}),-1.0]])]});
            var Q4;
            {var subQ0=sQuery(id+"F16.wireOp",EDGE,"55966892-68ea-4f88-a331-02177b37214e0.MirrorCS");Q4=makeQuery(id+"F16.imprint","IMPRINT",FACE,{"disambiguationData":[TD([[makeQuery(id+"F16.imprint","IMPRINT",EDGE,{"derivedFrom":subQ0}),-1.0]])]});}
            extrude(context, id + "F17", {"entities" : qUnion([Q0, Q1, Q2, Q3, Q4]), "operationType" : NewBodyOperationType.ADD, "depth" : 25 * mm});
        }
        {
            var Q0;
            Q0 = qSketchRegion(id + "F16", true);
            extrude(context, id + "F18", {"entities" : qUnion([Q0]), "operationType" : NewBodyOperationType.ADD, "depth" : 25 * mm});
        }
        {
            var Q0;
            Q0 = qSketchRegion(id + "F16", true);
            var Q1;
            {var subQ0=sQuery(id+"F16.wireOp",EDGE,"E86.MirrorCS");Q1=makeQuery(id+"F16.imprint","IMPRINT",FACE,{"disambiguationData":[TD([[makeQuery(id+"F16.imprint","IMPRINT",EDGE,{"derivedFrom":subQ0}),-1.0]])]});}
            extrude(context, id + "F19", {"entities" : qUnion([Q0, Q1]), "depth" : 25 * mm});
        }
    });
